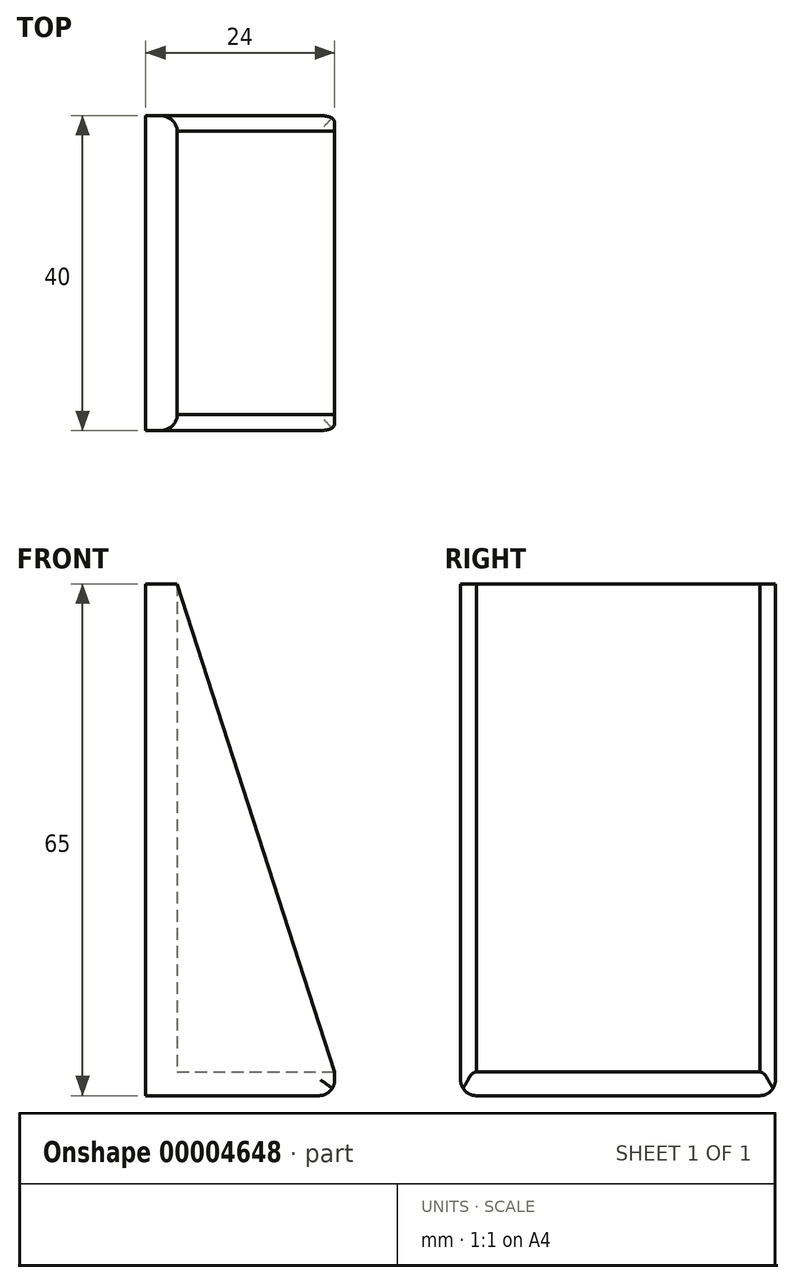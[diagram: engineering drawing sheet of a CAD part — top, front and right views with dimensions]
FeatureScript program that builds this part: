
annotation { "Feature Type Name" : "Feature", "Feature Type Description" : "" }
export const myFeature = defineFeature(function(context is Context, id is Id, definition is map)
    precondition{}
    {
        {
            var Q0;
            Q0=qCreatedBy(makeId("Front.planeOp"),FACE);
            var sketch = newSketch(context, id + "F0", { "sketchPlane" : qUnion([Q0])});
            skLineSegment(sketch, "E0.bottom", {"start": v(-10.04, 0) * mm, "end": v(9.96, 0) * mm});
            skLineSegment(sketch, "E0.top", {"start": v(-10.04, 40) * mm, "end": v(9.96, 40) * mm});
            skLineSegment(sketch, "E0.left", {"start": v(-10.04, 0) * mm, "end": v(-10.04, 40) * mm});
            skLineSegment(sketch, "E0.right", {"start": v(9.96, 0) * mm, "end": v(9.96, 40) * mm});
            skLineSegment(sketch, "E1.bottom", {"start": v(-10.04, 40) * mm, "end": v(-14.04, 40) * mm});
            skLineSegment(sketch, "E1.top", {"start": v(-10.04, 0) * mm, "end": v(-14.04, 0) * mm});
            skLineSegment(sketch, "E1.left", {"start": v(-10.04, 40) * mm, "end": v(-10.04, 0) * mm});
            skLineSegment(sketch, "E1.right", {"start": v(-14.04, 40) * mm, "end": v(-14.04, 0) * mm});
            skSolve(sketch);
        }
        {
            var Q0;
            Q0=makeQuery(id+"F0.imprint","IMPRINT",FACE,{"disambiguationData":[TD([[makeQuery(id+"F0.imprint","IMPRINT",EDGE,{"derivedFrom":sQuery(id+"F0.wireOp",EDGE,"E0.bottom")}),1.0]])]});
            extrude(context, id + "F1", {"entities" : qUnion([Q0]), "depth" : 3 * mm});
        }
        {
            var Q0;
            Q0=makeQuery(id+"F0.imprint","IMPRINT",FACE,{"disambiguationData":[TD([[makeQuery(id+"F0.imprint","IMPRINT",EDGE,{"derivedFrom":sQuery(id+"F0.wireOp",EDGE,"E1.bottom")}),1.0]])]});
            extrude(context, id + "F2", {"entities" : qUnion([Q0]), "operationType" : NewBodyOperationType.ADD, "depth" : 65 * mm});
        }
        {
            var Q0;
            Q0=makeQuery(id+"F1.opExtrude","SWEPT_BODY",BODY,{"disambiguationData":[OSD([sQuery(id+"F0.wireOp",EDGE,"E0.bottom"),sQuery(id+"F0.wireOp",EDGE,"E0.top"),sQuery(id+"F0.wireOp",EDGE,"E0.right"),sQuery(id+"F0.wireOp",EDGE,"E1.left")])]});
            var Q1;
            Q1=sQuery(id+"F0.wireOp",EDGE,"E0.bottom");
            transform(context, id + "F3", {"entities" : qUnion([Q0]), "transformType" : TransformType.ROTATION, "transformAxis" : qUnion([Q1]), "angle" : 90 * degree, "oppositeDirection" : true, "makeCopy" : false});
        }
        {
            var Q0;
            Q0=makeQuery(id+"F2.boolean.opBoolean","MERGE",FACE,{"derivedFrom":[makeQuery(id+"F1.opExtrude","SWEPT_FACE",FACE,{"disambiguationData":[OSD([sQuery(id+"F0.wireOp",EDGE,"E0.bottom")])]}),makeQuery(id+"F2.opExtrude","SWEPT_FACE",FACE,{"disambiguationData":[OSD([sQuery(id+"F0.wireOp",EDGE,"E1.top")])]})]});
            var sketch = newSketch(context, id + "F4", { "sketchPlane" : qUnion([Q0])});
            skLineSegment(sketch, "E2", {"start": v(-10.04, 65) * mm, "end": v(9.96, 3) * mm});
            skSolve(sketch);
        }
        {
            var Q0;
            Q0=makeQuery(id+"F4.imprint","IMPRINT",FACE,{"disambiguationData":[TD([[makeQuery(id+"F4.imprint","IMPRINT",EDGE,{"derivedFrom":sQuery(id+"F4.wireOp",EDGE,"E2")}),-1.0]])]});
            extrude(context, id + "F5", {"entities" : qUnion([Q0]), "operationType" : NewBodyOperationType.ADD, "oppositeDirection" : true, "depth" : 2 * mm});
        }
        {
            var Q0;
            Q0=makeQuery(id+"F2.boolean.opBoolean","MERGE",FACE,{"derivedFrom":[makeQuery(id+"F1.opExtrude","SWEPT_FACE",FACE,{"disambiguationData":[OSD([sQuery(id+"F0.wireOp",EDGE,"E0.top")])]}),makeQuery(id+"F2.opExtrude","SWEPT_FACE",FACE,{"disambiguationData":[OSD([sQuery(id+"F0.wireOp",EDGE,"E1.bottom")])]})]});
            var sketch = newSketch(context, id + "F6", { "sketchPlane" : qUnion([Q0])});
            skLineSegment(sketch, "E3", {"start": v(10.04, 65) * mm, "end": v(-9.96, 3) * mm});
            skSolve(sketch);
        }
        {
            var Q0;
            Q0=makeQuery(id+"F6.imprint","IMPRINT",FACE,{"disambiguationData":[TD([[makeQuery(id+"F6.imprint","IMPRINT",EDGE,{"derivedFrom":sQuery(id+"F6.wireOp",EDGE,"E3")}),1.0]])]});
            extrude(context, id + "F7", {"entities" : qUnion([Q0]), "operationType" : NewBodyOperationType.ADD, "oppositeDirection" : true, "depth" : 2 * mm});
        }
        {
            var Q0;
            Q0=makeQuery(id+"F5.opExtrude","CAP_EDGE",EDGE,{"disambiguationData":[OSD([sQuery(id+"F4.wireOp",EDGE,"E2")])],"isStart":true});
            var Q1;
            Q1=makeQuery(id+"F1.opExtrude","CAP_EDGE",EDGE,{"disambiguationData":[OSD([sQuery(id+"F0.wireOp",EDGE,"E0.right")])],"isStart":true});
            var Q2;
            Q2=makeQuery(id+"F7.opExtrude","CAP_EDGE",EDGE,{"disambiguationData":[OSD([sQuery(id+"F6.wireOp",EDGE,"E3")])],"isStart":true});
            var Q3;
            Q3=makeQuery(id+"F2.boolean.opBoolean","MERGE",EDGE,{"derivedFrom":[makeQuery(id+"F1.opExtrude","CAP_EDGE",EDGE,{"disambiguationData":[OSD([sQuery(id+"F0.wireOp",EDGE,"E0.bottom")])],"isStart":true}),makeQuery(id+"F2.opExtrude","CAP_EDGE",EDGE,{"disambiguationData":[OSD([sQuery(id+"F0.wireOp",EDGE,"E1.top")])],"isStart":true})]});
            var Q4;
            Q4=makeQuery(id+"F2.boolean.opBoolean","MERGE",EDGE,{"derivedFrom":[makeQuery(id+"F1.opExtrude","CAP_EDGE",EDGE,{"disambiguationData":[OSD([sQuery(id+"F0.wireOp",EDGE,"E0.top")])],"isStart":true}),makeQuery(id+"F2.opExtrude","CAP_EDGE",EDGE,{"disambiguationData":[OSD([sQuery(id+"F0.wireOp",EDGE,"E1.bottom")])],"isStart":true})]});
            fillet(context, id + "F8", {"entities" : qUnion([Q0, Q1, Q2, Q3, Q4]), "radius" : 2 * mm, "tangentPropagation" : true, "allowEdgeOverflow" : false});
        }
    });
